# Revit family: KO1000001_SUBCJ_GF_LVM_MonocKoral_Corona
name_source: partatom
category: Plumbing Fixtures
units: mm (PartAtom-declared; Revit-internal decimal feet)

## family parameters
Always vertical = Yes
Cut with Voids When Loaded = No
OmniClass Number = 23.31.11
Part Type = Normal
Room Calculation Point = No
Round Connector Dimension = Use Diameter
Shared = No
Work Plane-Based = No

## types (1)
- KO1000001_SUBCJ_GF_LVM_MonocKoral_Corona
    Acabado = Corona_Cromado
    Alto = 306 mm
    Ancho = 178 mm
    Años de Garantía = 30 años
    Capacidad de flujo = 5,7 l/min.
    Caudal = 8.3
    Creado por = IDD
    Description = La línea Koral con hiperahorro cuenta con todos los atributos de diseño y funcionalidad que la hacen perfecta para soluciones en espacios actuales. La mejor opción para tu baño.
    Diámetro = 45 mm
    Fecha de creación = 10/08/2020
    Garantía Acabados = 5 años
    Manufacturer = Corona
    Presion maxima = 125psi.
    Presion minima = 20 psi (138 Kpa).
    Referencia = KO1000001
    Resistencia a la humedad = Resistente a la corrosión pelado y decoloración por agua
    Temperatura de uso = 66°C ± 6°C
    URL = https://corona.co
    Vida útil = 500000.

## geometry (parser evidence)
native form markers: Sweep x6
no freeform markers — native parametric forms only
